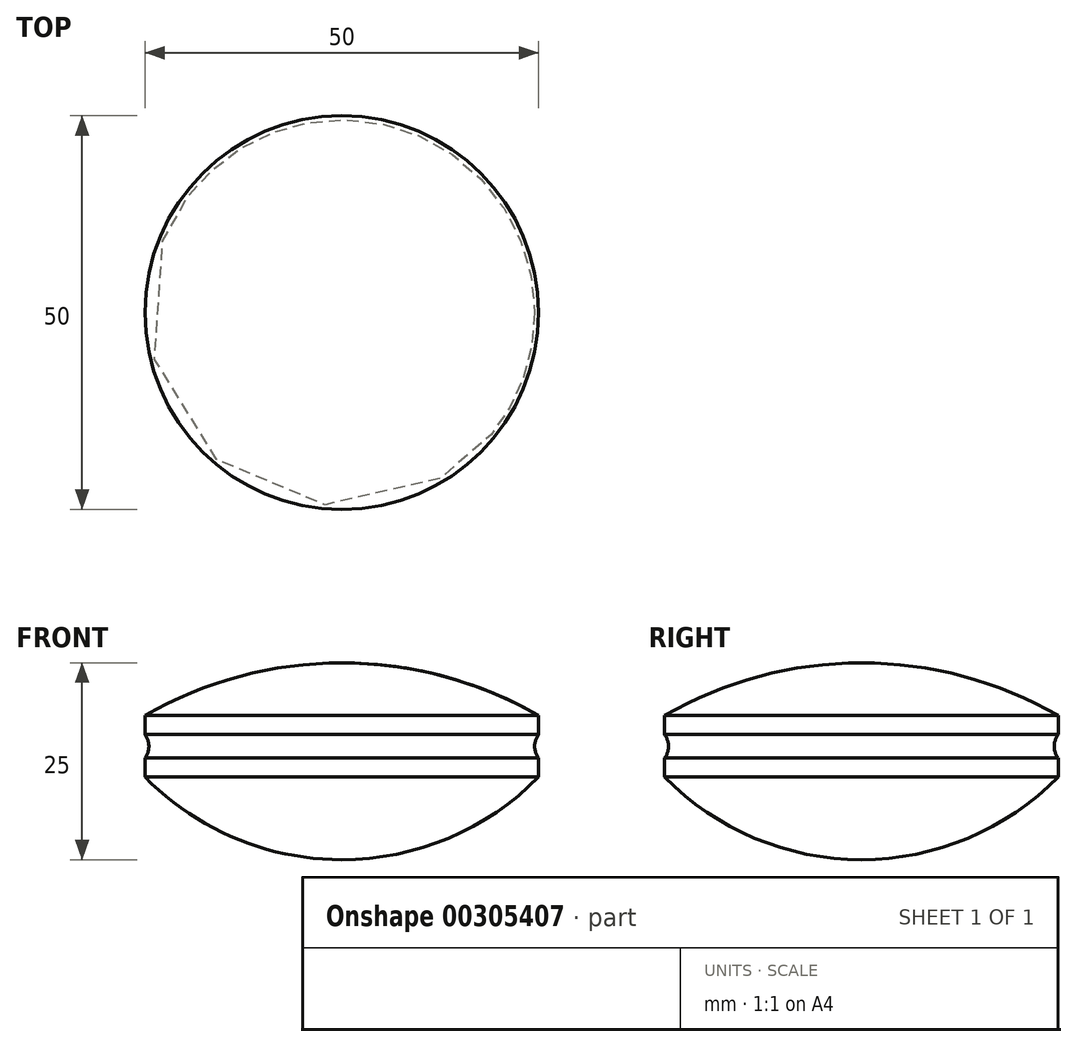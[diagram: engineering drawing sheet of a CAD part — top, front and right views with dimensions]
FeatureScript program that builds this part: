
annotation { "Feature Type Name" : "Feature", "Feature Type Description" : "" }
export const myFeature = defineFeature(function(context is Context, id is Id, definition is map)
    precondition{}
    {
        {
            var Q0;
            Q0=qCreatedBy(makeId("Front.planeOp"),FACE);
            var sketch = newSketch(context, id + "F0", { "sketchPlane" : qUnion([Q0])});
            skArc(sketch, "E0", {"start": v(0, 26.27) * mm, "mid": v(-12.94, 24.57) * mm, "end": v(-25, 19.57) * mm});
            skArc(sketch, "E1", {"start": v(-25, 11.78) * mm, "mid": v(-13.56, 4) * mm, "end": v(0, 1.27) * mm});
            skLineSegment(sketch, "E2", {"start": v(-25, 19.57) * mm, "end": v(-25, 11.78) * mm});
            skLineSegment(sketch, "E3", {"start": v(0, 26.27) * mm, "end": v(0, 1.27) * mm});
            skPoint(sketch, "E4.orphan", {"position": v(0, 33.34) * mm});
            skLineSegment(sketch, "E5", {"start": v(-25, 15.68) * mm, "end": v(-27, 15.68) * mm});
            skPoint(sketch, "E5.endSnap0", {"position": v(-25, 15.68) * mm});
            skCircle(sketch, "E6", {"center": v(-27, 15.68) * mm, "radius": 2.5 * mm});
            skSolve(sketch);
        }
        {
            var Q0;
            {var subQ0=sQuery(id+"F0.wireOp",EDGE,"E3");var subQ1=sQuery(id+"F0.wireOp",EDGE,"E0");var subQ2=makeQuery(id+"F0.imprint","INTERSECT",VERTEX,{"derivedFrom":[subQ1,subQ0]});Q0=makeQuery(id+"F0.imprint","IMPRINT",FACE,{"disambiguationData":[TD([[makeQuery(id+"F0.imprint","IMPRINT",EDGE,{"disambiguationData":[TD([[subQ2,-1.0]])],"derivedFrom":subQ1}),1.0]])]});}
            var Q1;
            Q1=sQuery(id+"F0.wireOp",EDGE,"E3");
            revolve(context, id + "F1", {"entities" : qUnion([Q0]), "axis" : qUnion([Q1]), "revolveType" : RevolveType.FULL});
        }
    });
